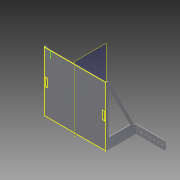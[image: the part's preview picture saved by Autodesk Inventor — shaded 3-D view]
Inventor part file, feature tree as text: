
AUTODESK INVENTOR PART (.ipt)
format: ipt  version: 2014 SP1 (Build 180222100, 222)  size: 364,032 bytes
history: native  units: in
note: dims shown in document units (in); Inventor stores cm internally (conversion verified against a paired STEP export)
features: sketch x12, other x12, sheet_metal_op x10, chamfer x3, pattern_linear x1, plane x1, mirror x1
ambient origin geometry x8: Origin, YZ Plane, XZ Plane, XY Plane, X Axis, Y Axis, Z Axis, Center Point
bodies: Solid1 (feature_tree)
feature tree (40):
  sheet_metal_op  "Face1"
  sheet_metal_op  "Flange1"
  sheet_metal_op  "Flange2"
  sheet_metal_op  "Flange3"
  chamfer  "Corner Round1"
  chamfer  "Corner Round2"
  chamfer  "Corner Round3"
  sketch  "Sketch12"  dims[d10=0.0625in]
  pattern_linear  "Rectangular Pattern2"  Spacing1=0.125in  [1 undecoded]
  plane  "Work Plane1"
  mirror  "Mirror1"
  sketch  "Sketch1"  dims[d0=7.1in]
  other  "Plate1"
  sketch  "Sketch2"  dims[d1=7.35in]
  other  "Plate2"
  sheet_metal_op  "Bend1"
  sheet_metal_op  "Corner1"
  sketch  "Sketch3"  dims[d2=0.125in]
  other  "Plate3"
  sheet_metal_op  "Bend2"
  sheet_metal_op  "Corner2"
  sketch  "Sketch4"  dims[d3=0.5in]
  other  "Plate4"
  sheet_metal_op  "Bend3"
  sheet_metal_op  "Corner3"
  sketch  "Sketch5"  dims[d4=0.25in]
  sketch  "Sketch6"  dims[d5=1.0in]
  sketch  "Sketch7"  dims[d6=0.125in]
  sketch  "Sketch8"  dims[d7=0.25in]
  sketch  "Sketch9"  dims[d8=1.0in]
  sketch  "Sketch10"  dims[d9=0.0625in]
  sketch  "Sketch14"  dims[d11=0.0312in d12=0.125in d13=0.0625in d14=3.5in d15=90.0deg d16=0.005in d17=0.25in d18=0.0625in d19=0.0625in d20=0.0625in d21=0.0312in d22=0.125in d23=0.0625in d24=3.5in d25=90.0deg d26=0.005in d27=0.25in d28=0.0625in d29=0.0625in d30=0.0625in d31=0.0312in d32=0.125in d33=0.0625in d34=3.5in d35=90.0deg d36=0.005in d37=0.25in d38=0.0625in d39=0.0625in d40=3.5625in d41=6.1in d42=0.25in d43=0.0in d44=3.563in d45=6.1in d46=0.25in d47=0.0in d48=0.25in d49=0.0625in d50=0.0in d51=0.25in d52=0.0625in d53=0.0in d54=0.125in d55=0.125in d56=0.25in d57=0.25in d58=0.25in d59=0.0625in d60=0.0in d61=0.0625in d62=0.0in d63=0.125in d66=0.375in d67=0.191in d68=0.0625in d69=0.0in d73=2.3622in d75=0.5in d76=3.66in]
  other  "Cut1"
  other  "Cut2"
  other  "Cut3"
  other  "Cut4"
  other  "Cut5"
  other  "Cut6"
  other  "Cut8"
  other  "Definition1"
note: 1 required parameter value undecoded (feature->parameter linkage not recoverable at this tier; creation-order binding heuristic only, values carry confidence <= 0.55)
